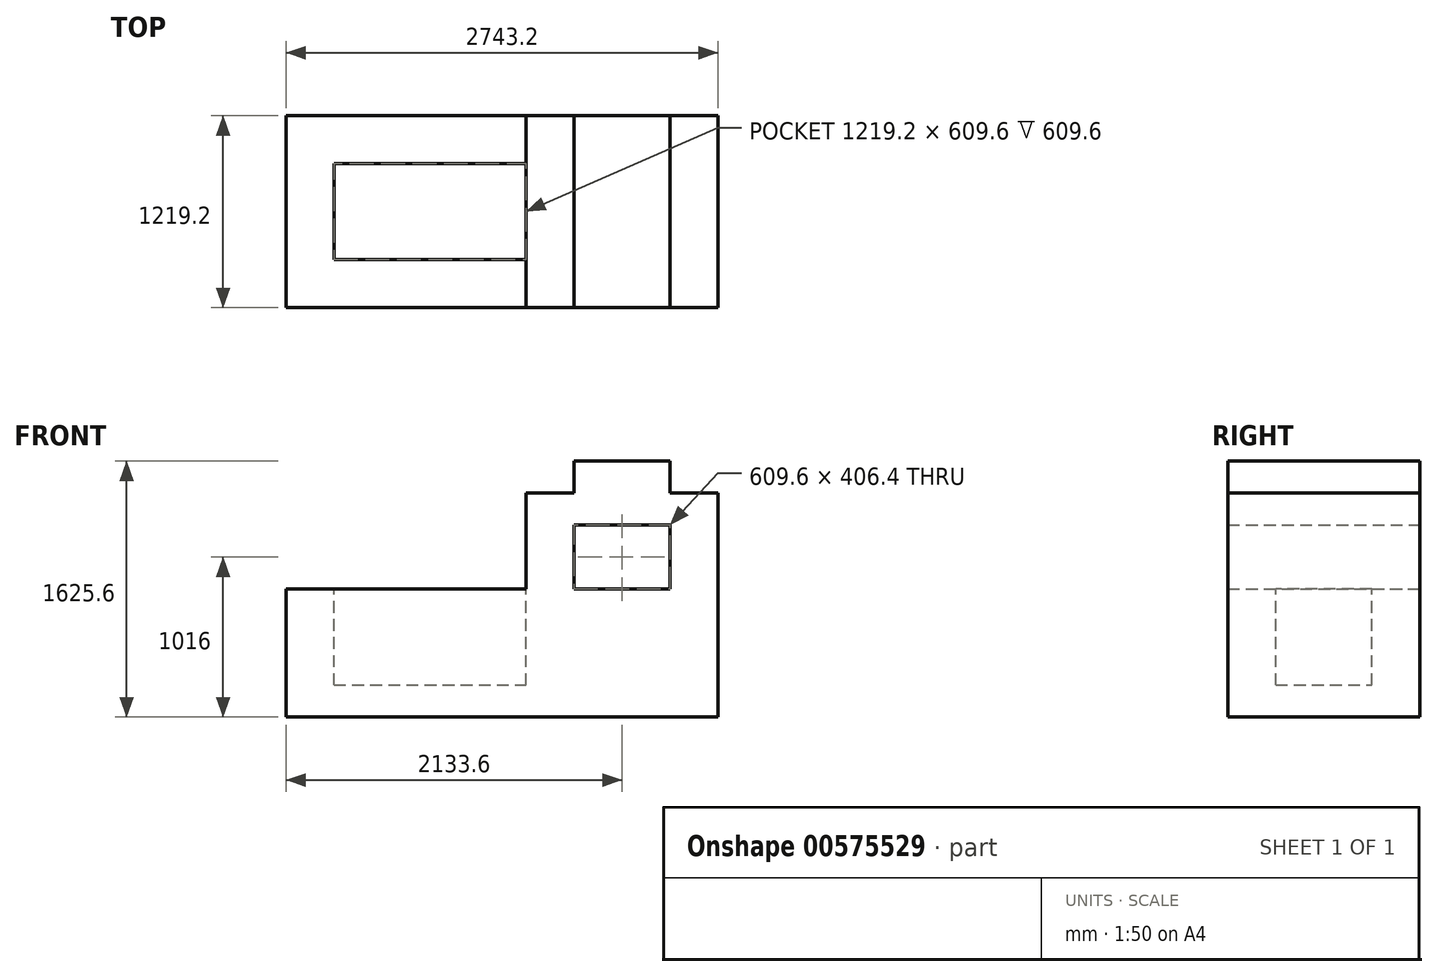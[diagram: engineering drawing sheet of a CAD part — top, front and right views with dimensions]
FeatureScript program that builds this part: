
annotation { "Feature Type Name" : "Feature", "Feature Type Description" : "" }
export const myFeature = defineFeature(function(context is Context, id is Id, definition is map)
    precondition{}
    {
        {
            var Q0;
            Q0=qCreatedBy(makeId("Front.planeOp"),FACE);
            var sketch = newSketch(context, id + "F0", { "sketchPlane" : qUnion([Q0])});
            skLineSegment(sketch, "E0", {"start": v(0, 0) * mm, "end": v(2743.2, 0) * mm});
            skLineSegment(sketch, "E1", {"start": v(2743.2, 0) * mm, "end": v(2743.2, 1422.4) * mm});
            skLineSegment(sketch, "E2", {"start": v(2743.2, 1422.4) * mm, "end": v(2438.4, 1422.4) * mm});
            skLineSegment(sketch, "E3", {"start": v(2438.4, 1422.4) * mm, "end": v(2438.4, 1625.6) * mm});
            skLineSegment(sketch, "E4", {"start": v(2438.4, 1625.6) * mm, "end": v(1828.8, 1625.6) * mm});
            skLineSegment(sketch, "E5", {"start": v(1828.8, 1625.6) * mm, "end": v(1828.8, 1422.4) * mm});
            skLineSegment(sketch, "E6", {"start": v(1828.8, 1422.4) * mm, "end": v(1524, 1422.4) * mm});
            skLineSegment(sketch, "E7", {"start": v(1524, 1422.4) * mm, "end": v(1524, 812.8) * mm});
            skLineSegment(sketch, "E8", {"start": v(1524, 812.8) * mm, "end": v(0, 812.8) * mm});
            skLineSegment(sketch, "E9", {"start": v(0, 812.8) * mm, "end": v(0, 0) * mm});
            skLineSegment(sketch, "E10", {"start": v(1828.8, 1219.2) * mm, "end": v(1828.8, 812.8) * mm});
            skLineSegment(sketch, "E11", {"start": v(1828.8, 812.8) * mm, "end": v(2438.4, 812.8) * mm});
            skLineSegment(sketch, "E12", {"start": v(2438.4, 812.8) * mm, "end": v(2438.4, 1219.2) * mm});
            skLineSegment(sketch, "E13", {"start": v(2438.4, 1219.2) * mm, "end": v(1828.8, 1219.2) * mm});
            skSolve(sketch);
        }
        {
            var Q0;
            Q0=makeQuery(id+"F0.imprint","IMPRINT",FACE,{"disambiguationData":[TD([[makeQuery(id+"F0.imprint","IMPRINT",EDGE,{"derivedFrom":sQuery(id+"F0.wireOp",EDGE,"E0")}),1.0]])]});
            extrude(context, id + "F1", {"entities" : qUnion([Q0]), "depth" : 1219.2 * mm, "offsetDistance" : 25.4 * mm});
        }
        {
            var Q0;
            Q0=makeQuery(id+"F1.opExtrude","SWEPT_FACE",FACE,{"disambiguationData":[OSD([sQuery(id+"F0.wireOp",EDGE,"E8")])]});
            var sketch = newSketch(context, id + "F2", { "sketchPlane" : qUnion([Q0])});
            skLineSegment(sketch, "E14", {"start": v(304.8, -304.8) * mm, "end": v(304.8, -914.4) * mm});
            skLineSegment(sketch, "E15", {"start": v(304.8, -914.4) * mm, "end": v(1524, -914.4) * mm});
            skLineSegment(sketch, "E16", {"start": v(1524, -914.4) * mm, "end": v(1524, -304.8) * mm});
            skLineSegment(sketch, "E17", {"start": v(1524, -304.8) * mm, "end": v(304.8, -304.8) * mm});
            skSolve(sketch);
        }
        {
            var Q0;
            Q0=makeQuery(id+"F2.imprint","IMPRINT",FACE,{"disambiguationData":[TD([[makeQuery(id+"F2.imprint","IMPRINT",EDGE,{"derivedFrom":sQuery(id+"F2.wireOp",EDGE,"E14")}),1.0]])]});
            extrude(context, id + "F3", {"entities" : qUnion([Q0]), "operationType" : NewBodyOperationType.REMOVE, "oppositeDirection" : true, "depth" : 609.6 * mm, "offsetDistance" : 25.4 * mm});
        }
    });
